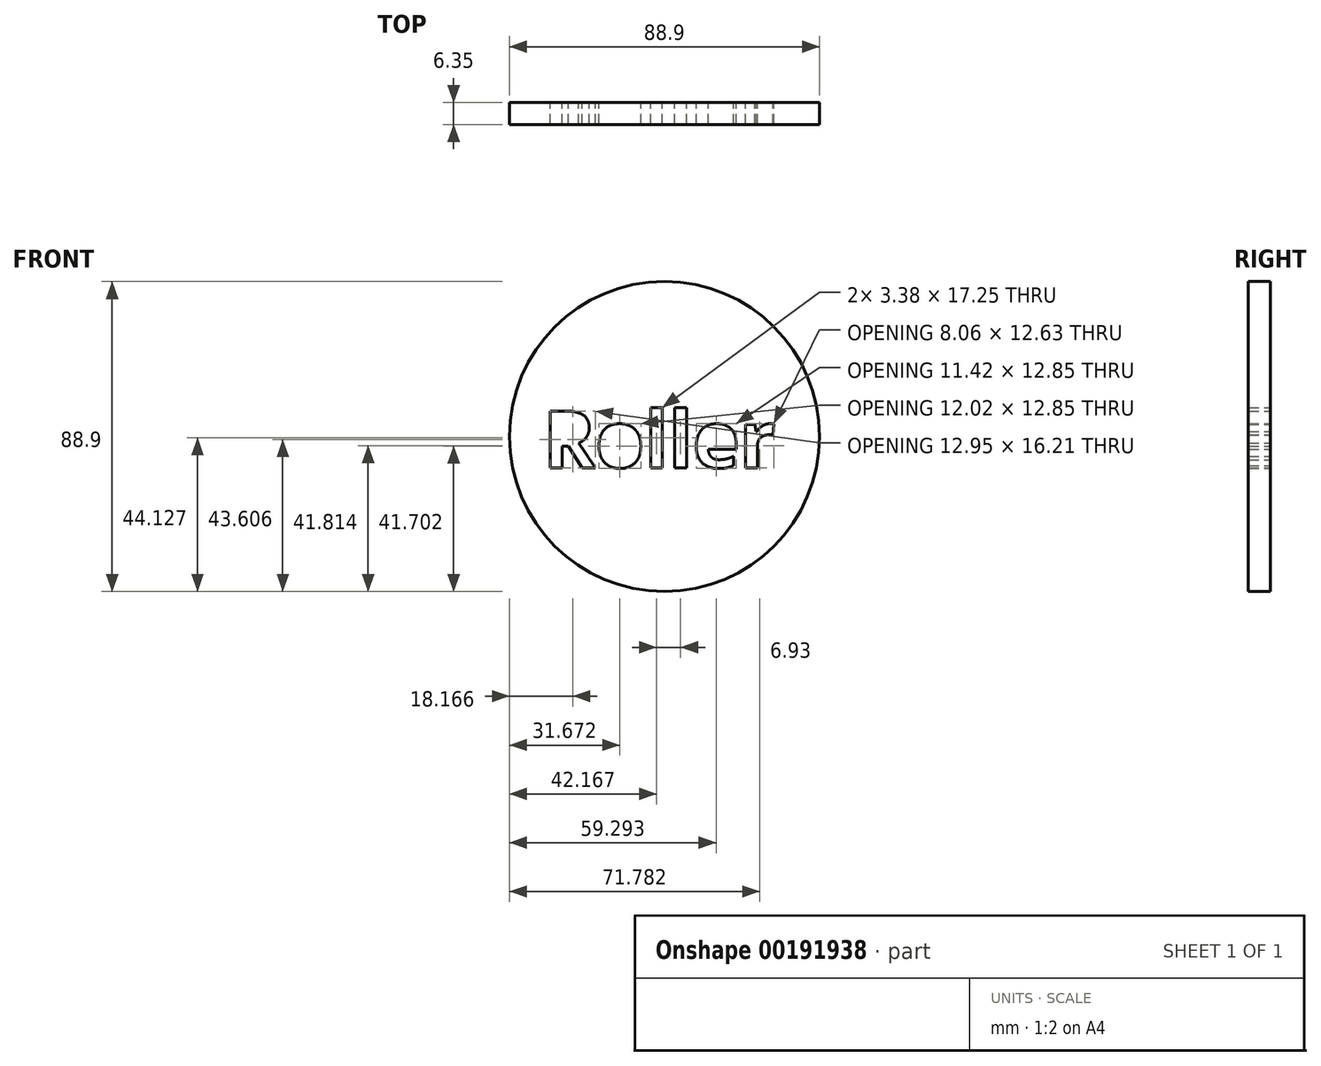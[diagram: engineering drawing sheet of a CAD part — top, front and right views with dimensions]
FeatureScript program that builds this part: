
annotation { "Feature Type Name" : "Feature", "Feature Type Description" : "" }
export const myFeature = defineFeature(function(context is Context, id is Id, definition is map)
    precondition{}
    {
        {
            var Q0;
            Q0=qCreatedBy(makeId("Front.planeOp"),FACE);
            var sketch = newSketch(context, id + "F0", { "sketchPlane" : qUnion([Q0])});
            skCircle(sketch, "E0", {"center": v(0, 0) * mm, "radius": 44.45 * mm});
            skText(sketch, "E1", { "text": "Roller", "fontName": "OpenSans-Bold.ttf"});
            const initialGuessF0  = {"E1": [-0.0348, -0.00895, 1, 0, 0.01635]};
            skSetInitialGuess(sketch, initialGuessF0);
            skSolve(sketch);
        }
        {
            var Q0;
            Q0 = qSketchRegion(id + "F0", true);
            extrude(context, id + "F1", {"entities" : qUnion([Q0]), "depth" : 6.35 * mm});
        }
    });
